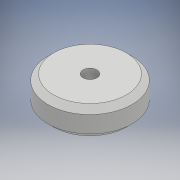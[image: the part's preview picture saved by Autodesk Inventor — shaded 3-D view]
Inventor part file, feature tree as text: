
AUTODESK INVENTOR PART (.ipt)
format: ipt  version: 2018.3 (Build 223284000, 284)  size: 104,448 bytes
history: native  units: mm
features: extrude x1, chamfer x1, sketch x1
ambient origin geometry x8: Origin, YZ Plane, XZ Plane, XY Plane, X Axis, Y Axis, Z Axis, Center Point
bodies: Solid1 (feature_tree)
feature tree (3):
  extrude  "Extrusion1"  Depth=10.0mm
  chamfer  "Chamfer1"  Distance=10.0mm
  sketch  "Sketch1"  dims[d0=5.0mm d1=30.0mm d2=10.0mm d3=0.0mm d4=2.0mm d5=2.0mm d6=45.0deg]
